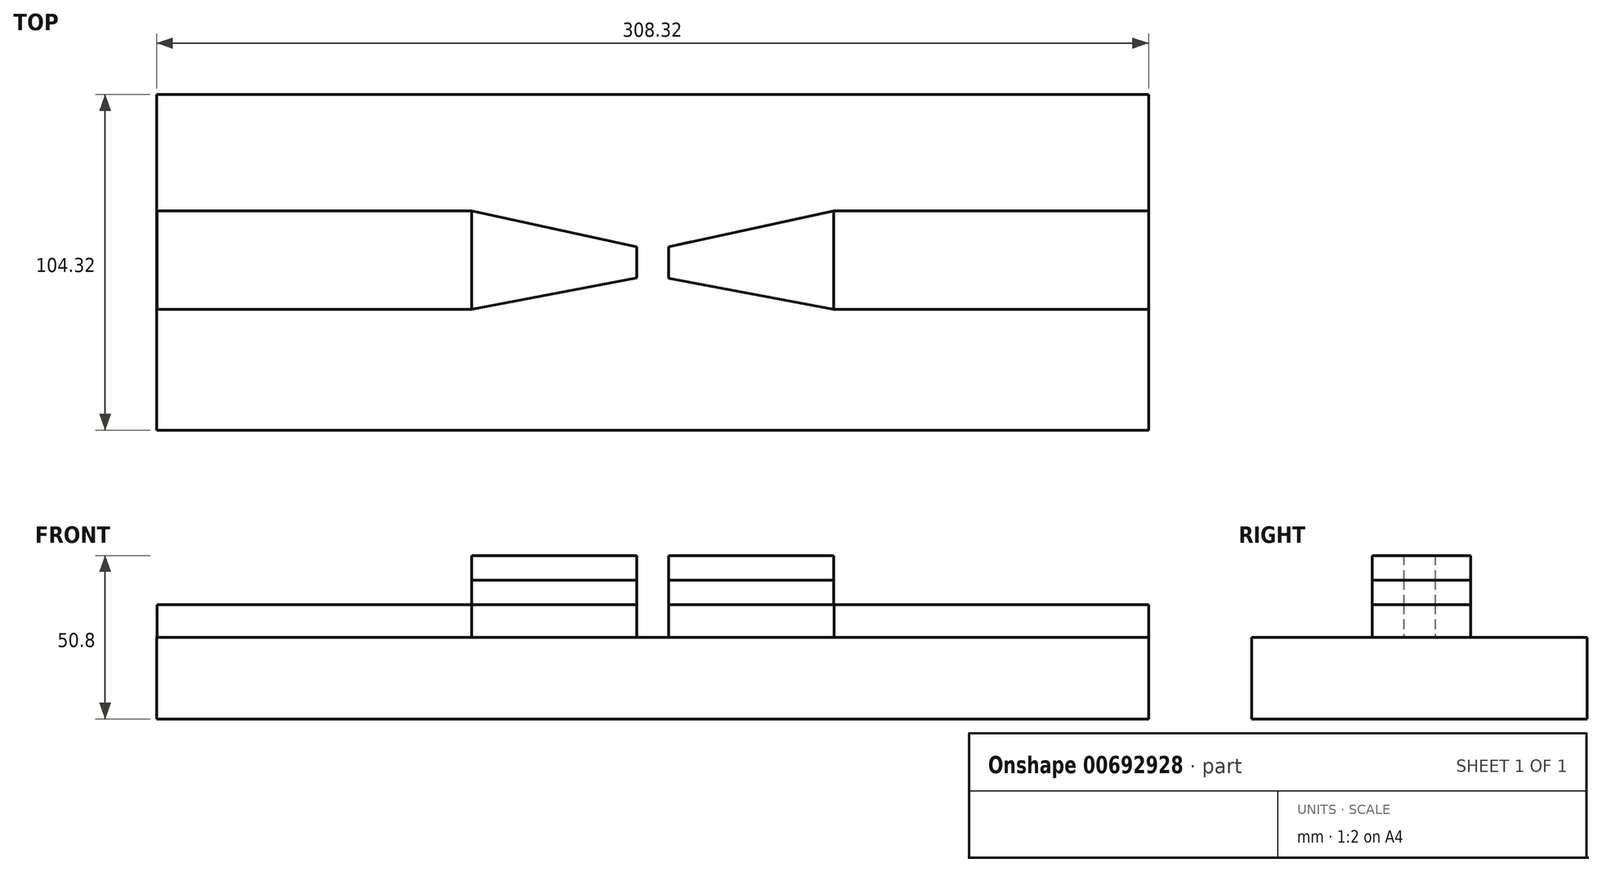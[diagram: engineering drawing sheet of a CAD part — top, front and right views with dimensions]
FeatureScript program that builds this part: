
annotation { "Feature Type Name" : "Feature", "Feature Type Description" : "" }
export const myFeature = defineFeature(function(context is Context, id is Id, definition is map)
    precondition{}
    {
        {
            var Q0;
            Q0=qCreatedBy(makeId("Top.planeOp"),FACE);
            var sketch = newSketch(context, id + "F0", { "sketchPlane" : qUnion([Q0])});
            skLineSegment(sketch, "E0.left", {"start": v(-149.3, 52.16) * mm, "end": v(-149.3, -52.16) * mm});
            skPoint(sketch, "E0.middle", {"position": v(0, 0) * mm});
            skLineSegment(sketch, "E1", {"start": v(-149.3, 52.16) * mm, "end": v(159.01, 52.16) * mm});
            skLineSegment(sketch, "E2", {"start": v(159.01, 52.16) * mm, "end": v(159.01, -52.16) * mm});
            skLineSegment(sketch, "E3", {"start": v(159.01, -52.16) * mm, "end": v(-149.3, -52.16) * mm});
            skSolve(sketch);
        }
        {
            var Q0;
            Q0=qSketchRegion(id+"F0",true);
            var Q1;
            Q1=makeQuery(id+"F0.imprint","IMPRINT",FACE,{"disambiguationData":[TD([[makeQuery(id+"F0.imprint","IMPRINT",EDGE,{"derivedFrom":sQuery(id+"F0.wireOp",EDGE,"E0.bottom")}),-1.0]])]});
            extrude(context, id + "F1", {"entities" : qUnion([Q0, Q1]), "oppositeDirection" : true, "depth" : 25.4 * mm, "offsetDistance" : 25.4 * mm});
        }
        {
            var Q0;
            Q0=makeQuery(id+"F1.opExtrude","CAP_FACE",FACE,{"disambiguationData":[OSD([sQuery(id+"F0.wireOp",EDGE,"E0.bottom"),sQuery(id+"F0.wireOp",EDGE,"E0.top"),sQuery(id+"F0.wireOp",EDGE,"E0.left"),sQuery(id+"F0.wireOp",EDGE,"E0.right")])],"isStart":true});
            var sketch = newSketch(context, id + "F2", { "sketchPlane" : qUnion([Q0])});
            skLineSegment(sketch, "E4", {"start": v(-51.41, 16.02) * mm, "end": v(0, 4.87) * mm});
            skLineSegment(sketch, "E5", {"start": v(0, 4.87) * mm, "end": v(0, -4.87) * mm});
            skLineSegment(sketch, "E6", {"start": v(0, -4.87) * mm, "end": v(-51.41, -14.6) * mm});
            skLineSegment(sketch, "E7", {"start": v(-51.41, 16.02) * mm, "end": v(-149.21, 16.02) * mm});
            skLineSegment(sketch, "E8", {"start": v(-149.21, 16.02) * mm, "end": v(-149.21, -14.6) * mm});
            skLineSegment(sketch, "E9", {"start": v(-149.21, -14.6) * mm, "end": v(-51.41, -14.6) * mm});
            skLineSegment(sketch, "E10", {"start": v(4.9, 43.5) * mm, "end": v(4.9, -44.34) * mm});
            skLineSegment(sketch, "E11.MirrorCS", {"start": v(61.22, 16.02) * mm, "end": v(159.02, 16.02) * mm});
            skLineSegment(sketch, "E12.MirrorCS", {"start": v(61.22, 16.02) * mm, "end": v(9.81, 4.87) * mm});
            skLineSegment(sketch, "E13.MirrorCS", {"start": v(9.81, 4.87) * mm, "end": v(9.81, -4.87) * mm});
            skLineSegment(sketch, "E14.MirrorCS", {"start": v(9.81, -4.87) * mm, "end": v(61.22, -14.6) * mm});
            skLineSegment(sketch, "E15.MirrorCS", {"start": v(159.02, -14.6) * mm, "end": v(61.22, -14.6) * mm});
            skLineSegment(sketch, "E16.MirrorCS", {"start": v(159.02, 16.02) * mm, "end": v(159.02, -14.6) * mm});
            skSolve(sketch);
        }
        {
            var Q0;
            Q0=qSketchRegion(id+"F2",true);
            extrude(context, id + "F3", {"entities" : qUnion([Q0]), "depth" : 10.16 * mm, "offsetDistance" : 25.4 * mm});
        }
        {
            var Q0;
            Q0=makeQuery(id+"F3.opExtrude","CAP_FACE",FACE,{"disambiguationData":[OSD([sQuery(id+"F2.wireOp",EDGE,"E4"),sQuery(id+"F2.wireOp",EDGE,"E5"),sQuery(id+"F2.wireOp",EDGE,"E6"),sQuery(id+"F2.wireOp",EDGE,"E7"),sQuery(id+"F2.wireOp",EDGE,"E8"),sQuery(id+"F2.wireOp",EDGE,"E9")])],"isStart":false});
            var sketch = newSketch(context, id + "F4", { "sketchPlane" : qUnion([Q0])});
            skLineSegment(sketch, "E17", {"start": v(-51.41, 16.02) * mm, "end": v(0, 4.87) * mm});
            skLineSegment(sketch, "E18", {"start": v(0, 4.87) * mm, "end": v(0, -4.87) * mm});
            skLineSegment(sketch, "E19", {"start": v(0, -4.87) * mm, "end": v(-51.41, -14.6) * mm});
            skLineSegment(sketch, "E20", {"start": v(-51.41, -14.6) * mm, "end": v(-51.41, 16.02) * mm});
            skLineSegment(sketch, "E21", {"start": v(9.82, 4.87) * mm, "end": v(9.82, -4.9) * mm});
            skLineSegment(sketch, "E22", {"start": v(9.82, -4.9) * mm, "end": v(61.21, -14.6) * mm});
            skLineSegment(sketch, "E23", {"start": v(61.21, -14.6) * mm, "end": v(61.21, 16.01) * mm});
            skLineSegment(sketch, "E24", {"start": v(61.21, 16.01) * mm, "end": v(9.82, 4.87) * mm});
            skSolve(sketch);
        }
        {
            var Q0;
            Q0=qSketchRegion(id+"F4",true);
            extrude(context, id + "F5", {"entities" : qUnion([Q0]), "depth" : 7.62 * mm, "offsetDistance" : 25.4 * mm});
        }
        {
            var Q0;
            Q0=makeQuery(id+"F5.opExtrude","CAP_FACE",FACE,{"disambiguationData":[OSD([sQuery(id+"F4.wireOp",EDGE,"E17"),sQuery(id+"F4.wireOp",EDGE,"E18"),sQuery(id+"F4.wireOp",EDGE,"E19"),sQuery(id+"F4.wireOp",EDGE,"E20")])],"isStart":false});
            var sketch = newSketch(context, id + "F6", { "sketchPlane" : qUnion([Q0])});
            skLineSegment(sketch, "E25", {"start": v(-51.41, 16.02) * mm, "end": v(0, 4.87) * mm});
            skLineSegment(sketch, "E26", {"start": v(0, 4.87) * mm, "end": v(0, -4.87) * mm});
            skLineSegment(sketch, "E27", {"start": v(0, -4.87) * mm, "end": v(-51.41, -14.6) * mm});
            skLineSegment(sketch, "E28", {"start": v(-51.41, -14.6) * mm, "end": v(-51.41, 16.02) * mm});
            skLineSegment(sketch, "E29", {"start": v(9.82, 4.87) * mm, "end": v(9.82, -4.9) * mm});
            skLineSegment(sketch, "E30", {"start": v(9.82, -4.9) * mm, "end": v(61.2, -14.6) * mm});
            skLineSegment(sketch, "E31", {"start": v(61.2, -14.6) * mm, "end": v(61.2, 16.01) * mm});
            skLineSegment(sketch, "E32", {"start": v(61.2, 16.01) * mm, "end": v(9.82, 4.87) * mm});
            skSolve(sketch);
        }
        {
            var Q0;
            Q0=qSketchRegion(id+"F6",true);
            extrude(context, id + "F7", {"entities" : qUnion([Q0]), "depth" : 7.62 * mm, "offsetDistance" : 25.4 * mm});
        }
    });
